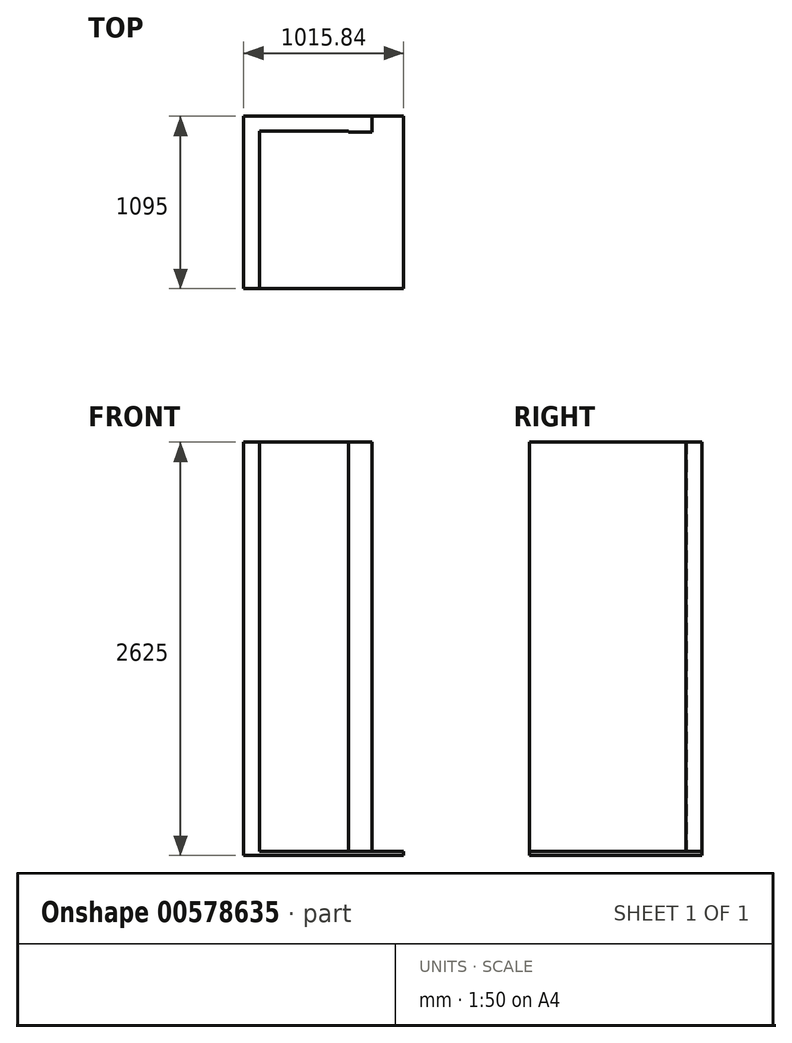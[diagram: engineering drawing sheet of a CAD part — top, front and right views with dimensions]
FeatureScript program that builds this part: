
annotation { "Feature Type Name" : "Feature", "Feature Type Description" : "" }
export const myFeature = defineFeature(function(context is Context, id is Id, definition is map)
    precondition{}
    {
        {
            var Q0;
            Q0=qCreatedBy(makeId("Top.planeOp"),FACE);
            var sketch = newSketch(context, id + "F0", { "sketchPlane" : qUnion([Q0])});
            skLineSegment(sketch, "E0", {"start": v(0, 0) * mm, "end": v(0, 1000) * mm});
            skLineSegment(sketch, "E1", {"start": v(0, 1000) * mm, "end": v(565, 1000) * mm});
            skLineSegment(sketch, "E2", {"start": v(565, 1000) * mm, "end": v(565, 995) * mm});
            skLineSegment(sketch, "E3", {"start": v(565, 995) * mm, "end": v(715, 995) * mm});
            skLineSegment(sketch, "E4", {"start": v(715, 995) * mm, "end": v(715, 1095) * mm});
            skLineSegment(sketch, "E5", {"start": v(715, 1095) * mm, "end": v(-100, 1095) * mm});
            skLineSegment(sketch, "E6", {"start": v(-100, 1095) * mm, "end": v(-100, 0) * mm});
            skLineSegment(sketch, "E7", {"start": v(-100, 0) * mm, "end": v(0, 0) * mm});
            skSolve(sketch);
        }
        {
            var Q0;
            Q0 = qSketchRegion(id + "F0", true);
            extrude(context, id + "F1", {"entities" : qUnion([Q0]), "depth" : 2600 * mm, "offsetDistance" : 25 * mm});
        }
        {
            var Q0;
            Q0=makeQuery(id+"F1.opExtrude","CAP_FACE",FACE,{"disambiguationData":[OSD([sQuery(id+"F0.wireOp",EDGE,"E0"),sQuery(id+"F0.wireOp",EDGE,"E1"),sQuery(id+"F0.wireOp",EDGE,"E2"),sQuery(id+"F0.wireOp",EDGE,"E3"),sQuery(id+"F0.wireOp",EDGE,"E4"),sQuery(id+"F0.wireOp",EDGE,"E5"),sQuery(id+"F0.wireOp",EDGE,"E6"),sQuery(id+"F0.wireOp",EDGE,"E7")])],"isStart":true});
            var sketch = newSketch(context, id + "F2", { "sketchPlane" : qUnion([Q0])});
            skLineSegment(sketch, "E8.bottom", {"start": v(-100, 0) * mm, "end": v(915.84, 0) * mm});
            skLineSegment(sketch, "E8.top", {"start": v(-100, -1095) * mm, "end": v(915.84, -1095) * mm});
            skLineSegment(sketch, "E8.left", {"start": v(-100, 0) * mm, "end": v(-100, -1095) * mm});
            skLineSegment(sketch, "E8.right", {"start": v(915.84, 0) * mm, "end": v(915.84, -1095) * mm});
            skSolve(sketch);
        }
        {
            var Q0;
            Q0 = qSketchRegion(id + "F2", true);
            extrude(context, id + "F3", {"entities" : qUnion([Q0]), "operationType" : NewBodyOperationType.ADD, "depth" : 25 * mm, "offsetDistance" : 25 * mm});
        }
    });
